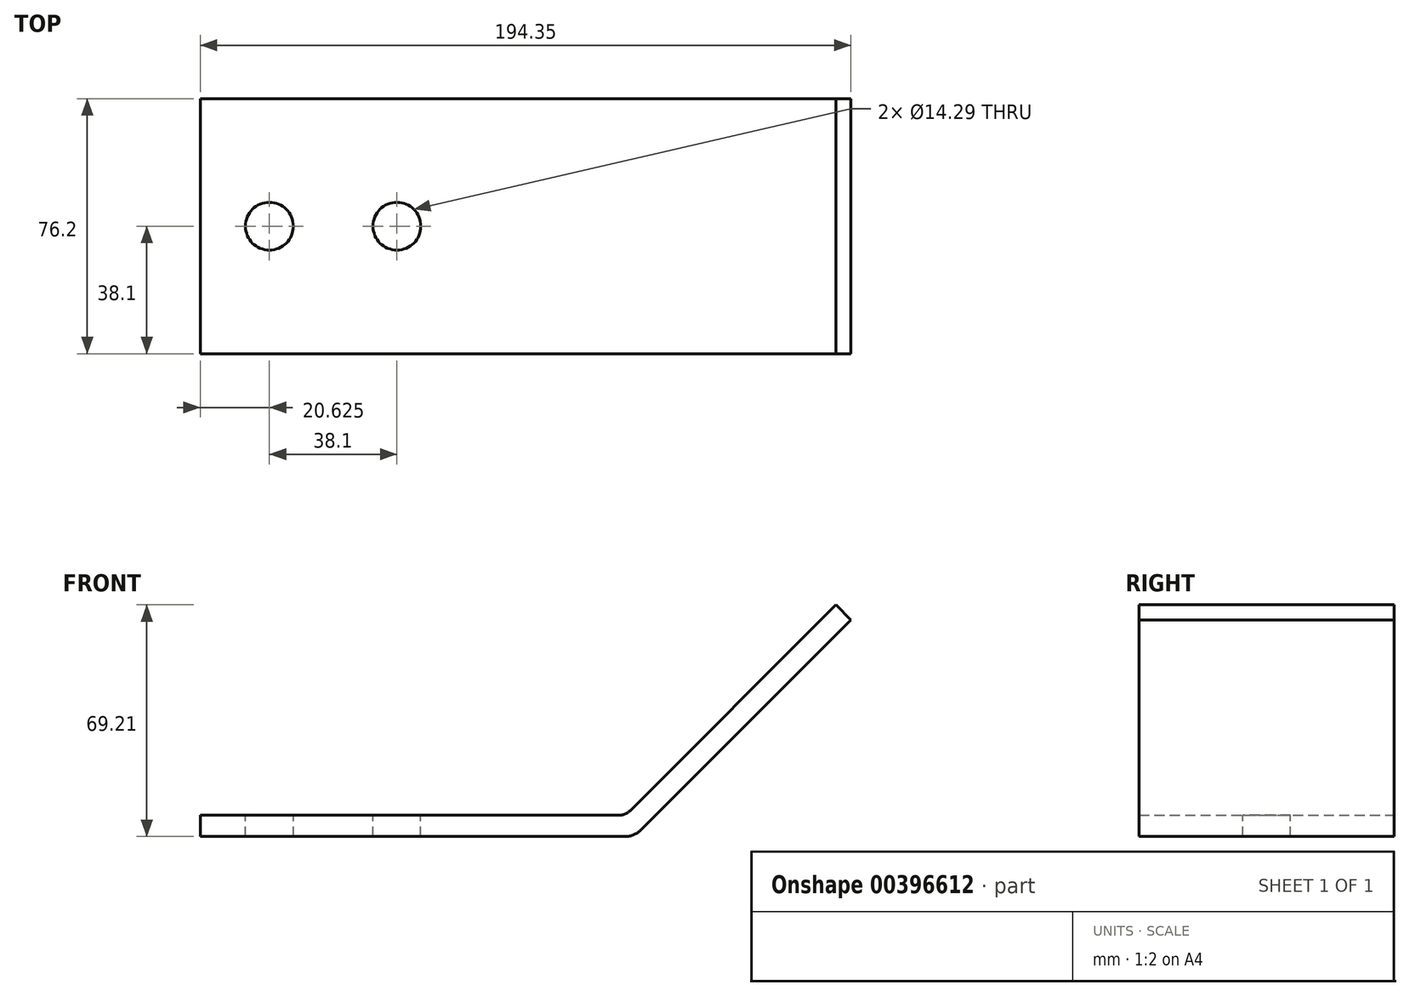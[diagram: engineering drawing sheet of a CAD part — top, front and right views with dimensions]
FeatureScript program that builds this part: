
annotation { "Feature Type Name" : "Feature", "Feature Type Description" : "" }
export const myFeature = defineFeature(function(context is Context, id is Id, definition is map)
    precondition{}
    {
        {
            var Q0;
            Q0=qCreatedBy(makeId("Front.planeOp"),FACE);
            var sketch = newSketch(context, id + "F0", { "sketchPlane" : qUnion([Q0])});
            skLineSegment(sketch, "E0.bottom", {"start": v(0, 0) * mm, "end": v(-127, 0) * mm});
            skLineSegment(sketch, "E0.top", {"start": v(0, 6.35) * mm, "end": v(-127, 6.35) * mm});
            skLineSegment(sketch, "E0.right", {"start": v(-127, 0) * mm, "end": v(-127, 6.35) * mm});
            skLineSegment(sketch, "E1", {"start": v(0, 6.35) * mm, "end": v(62.86, 69.21) * mm});
            skLineSegment(sketch, "E2", {"start": v(62.86, 69.21) * mm, "end": v(67.35, 64.72) * mm});
            skLineSegment(sketch, "E3", {"start": v(67.35, 64.72) * mm, "end": v(4.5, 1.86) * mm});
            skLineSegment(sketch, "E4", {"start": v(4.5, 1.86) * mm, "end": v(2.63, 0) * mm});
            skLineSegment(sketch, "E5", {"start": v(2.63, 0) * mm, "end": v(0, 0) * mm});
            skSolve(sketch);
        }
        {
            var Q0;
            Q0 = qSketchRegion(id + "F0", true);
            extrude(context, id + "F1", {"entities" : qUnion([Q0]), "depth" : 76.2 * mm});
        }
        {
            var Q0;
            Q0=makeQuery(id+"F1.opExtrude","SWEPT_EDGE",EDGE,{"disambiguationData":[OSD([sQuery(id+"F0.wireOp",EDGE,"E0.top"),sQuery(id+"F0.wireOp",EDGE,"E1")])]});
            fillet(context, id + "F2", {"entities" : qUnion([Q0]), "radius" : 5.08 * mm, "tangentPropagation" : true, "allowEdgeOverflow" : false});
        }
        {
            var Q0;
            Q0=makeQuery(id+"F1.opExtrude","SWEPT_EDGE",EDGE,{"disambiguationData":[OSD([sQuery(id+"F0.wireOp",EDGE,"E4"),sQuery(id+"F0.wireOp",EDGE,"E5")])]});
            fillet(context, id + "F3", {"entities" : qUnion([Q0]), "radius" : 6.35 * mm, "tangentPropagation" : true, "allowEdgeOverflow" : false});
        }
        {
            var Q0;
            Q0=makeQuery(id+"F1.opExtrude","SWEPT_FACE",FACE,{"disambiguationData":[OSD([sQuery(id+"F0.wireOp",EDGE,"E0.top")])]});
            var sketch = newSketch(context, id + "F4", { "sketchPlane" : qUnion([Q0])});
            skCircle(sketch, "E6", {"center": v(-106.38, -38.1) * mm, "radius": 7.14 * mm});
            skPoint(sketch, "E6.centerSnap0", {"position": v(-127, -38.1) * mm});
            skCircle(sketch, "E7", {"center": v(-68.28, -38.1) * mm, "radius": 7.14 * mm});
            skSolve(sketch);
        }
        {
            var Q0;
            Q0 = qSketchRegion(id + "F4", true);
            extrude(context, id + "F5", {"entities" : qUnion([Q0]), "operationType" : NewBodyOperationType.REMOVE, "oppositeDirection" : true, "depth" : 25.4 * mm});
        }
    });
